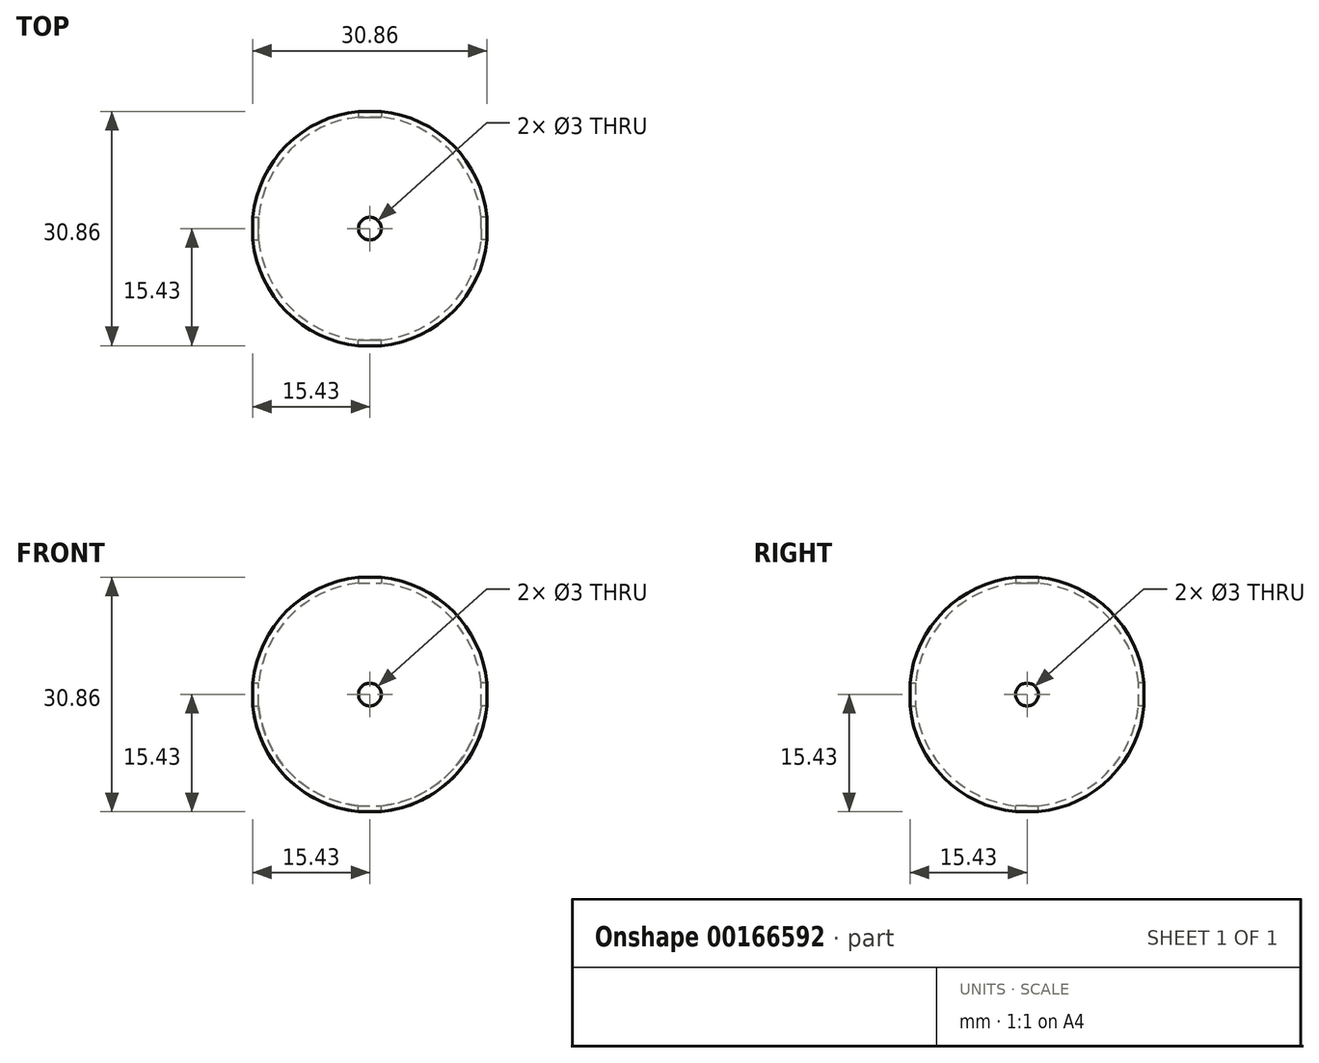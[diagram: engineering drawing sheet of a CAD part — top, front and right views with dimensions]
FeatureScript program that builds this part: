
annotation { "Feature Type Name" : "Feature", "Feature Type Description" : "" }
export const myFeature = defineFeature(function(context is Context, id is Id, definition is map)
    precondition{}
    {
        {
            var Q0;
            Q0=qCreatedBy(makeId("Top.planeOp"),FACE);
            var sketch = newSketch(context, id + "F0", { "sketchPlane" : qUnion([Q0])});
            skLineSegment(sketch, "E0", {"start": v(-18.23, 0) * mm, "end": v(19.4, 0) * mm});
            skArc(sketch, "E1", {"start": v(15.5, 0) * mm, "mid": v(0, 15.5) * mm, "end": v(-15.5, 0) * mm});
            skSolve(sketch);
        }
        {
            var Q0;
            {var subQ0=sQuery(id+"F0.wireOp",EDGE,"E1");Q0=makeQuery(id+"F0.imprint","IMPRINT",FACE,{"disambiguationData":[TD([[makeQuery(id+"F0.imprint","IMPRINT",EDGE,{"derivedFrom":subQ0}),1.0]])]});}
            var Q1;
            Q1 = qSketchRegion(id + "F3", true);
            var Q2;
            Q2=sQuery(id+"F0.wireOp",EDGE,"E0");
            revolve(context, id + "F1", {"entities" : qUnion([Q0, Q1]), "axis" : qUnion([Q2]), "revolveType" : RevolveType.FULL});
        }
        {
            var Q0;
            Q0=makeQuery(id+"F1.opRevolve","SWEPT_FACE",FACE,{"disambiguationData":[OSD([sQuery(id+"F0.wireOp",EDGE,"E1")])]});
            var Q1;
            Q1=makeQuery(id+"F1.opRevolve","SWEPT_BODY",BODY,{"disambiguationData":[OSD([sQuery(id+"F0.wireOp",EDGE,"E0"),sQuery(id+"F0.wireOp",EDGE,"E1")])]});
            shell(context, id + "F2", {"isHollow" : true, "entities" : qUnion([Q0]), "parts" : qUnion([Q1]), "thickness" : .75 * mm});
        }
        {
            var Q0;
            Q0=qCreatedBy(makeId("Top.planeOp"),FACE);
            var sketch = newSketch(context, id + "F3", { "sketchPlane" : qUnion([Q0])});
            skPoint(sketch, "E2", {"position": v(0, 0) * mm});
            skSolve(sketch);
        }
        {
            var Q0;
            Q0=sQuery(id+"F3.wireOp",VERTEX,"E2");
            var Q1;
            Q1=makeQuery(id+"F1.opRevolve","SWEPT_BODY",BODY,{"disambiguationData":[OSD([sQuery(id+"F0.wireOp",EDGE,"E0"),sQuery(id+"F0.wireOp",EDGE,"E1")])]});
            hole(context, id + "F4", {"style" : HoleStyle.SIMPLE, "endStyle" : HoleEndStyle.THROUGH, "holeDiameter" : 3 * mm, "locations" : qUnion([Q0]), "scope" : qUnion([Q1]), "isTappedThrough" : true});
        }
        {
            var Q0;
            Q0=qCreatedBy(makeId("Top.planeOp"),FACE);
            var sketch = newSketch(context, id + "F5", { "sketchPlane" : qUnion([Q0])});
            skPoint(sketch, "E3", {"position": v(0, 0) * mm});
            skSolve(sketch);
        }
        {
            var Q0;
            Q0=sQuery(id+"F5.wireOp",VERTEX,"E3");
            var Q1;
            Q1=makeQuery(id+"F1.opRevolve","SWEPT_BODY",BODY,{"disambiguationData":[OSD([sQuery(id+"F0.wireOp",EDGE,"E0"),sQuery(id+"F0.wireOp",EDGE,"E1")])]});
            hole(context, id + "F6", {"style" : HoleStyle.SIMPLE, "endStyle" : HoleEndStyle.THROUGH, "oppositeDirection" : true, "holeDiameter" : 3 * mm, "locations" : qUnion([Q0]), "scope" : qUnion([Q1]), "isTappedThrough" : true});
        }
        {
            var Q0;
            Q0=qCreatedBy(makeId("Right.planeOp"),FACE);
            var sketch = newSketch(context, id + "F7", { "sketchPlane" : qUnion([Q0])});
            skPoint(sketch, "E4", {"position": v(0, 0) * mm});
            skSolve(sketch);
        }
        {
            var Q0;
            Q0=sQuery(id+"F7.wireOp",VERTEX,"E4");
            var Q1;
            Q1=makeQuery(id+"F1.opRevolve","SWEPT_BODY",BODY,{"disambiguationData":[OSD([sQuery(id+"F0.wireOp",EDGE,"E0"),sQuery(id+"F0.wireOp",EDGE,"E1")])]});
            hole(context, id + "F8", {"style" : HoleStyle.SIMPLE, "endStyle" : HoleEndStyle.THROUGH, "holeDiameter" : 3 * mm, "locations" : qUnion([Q0]), "scope" : qUnion([Q1]), "isTappedThrough" : true});
        }
        {
            var Q0;
            Q0=qCreatedBy(makeId("Right.planeOp"),FACE);
            var sketch = newSketch(context, id + "F9", { "sketchPlane" : qUnion([Q0])});
            skPoint(sketch, "E5", {"position": v(0, 0) * mm});
            skSolve(sketch);
        }
        {
            var Q0;
            Q0=sQuery(id+"F9.wireOp",VERTEX,"E5");
            var Q1;
            Q1=makeQuery(id+"F1.opRevolve","SWEPT_BODY",BODY,{"disambiguationData":[OSD([sQuery(id+"F0.wireOp",EDGE,"E0"),sQuery(id+"F0.wireOp",EDGE,"E1")])]});
            hole(context, id + "F10", {"style" : HoleStyle.SIMPLE, "endStyle" : HoleEndStyle.THROUGH, "oppositeDirection" : true, "holeDiameter" : 3 * mm, "locations" : qUnion([Q0]), "scope" : qUnion([Q1]), "isTappedThrough" : true});
        }
        {
            var Q0;
            Q0=qCreatedBy(makeId("Front.planeOp"),FACE);
            var sketch = newSketch(context, id + "F11", { "sketchPlane" : qUnion([Q0])});
            skPoint(sketch, "E6", {"position": v(0, 0) * mm});
            skSolve(sketch);
        }
        {
            var Q0;
            Q0=sQuery(id+"F11.wireOp",VERTEX,"E6");
            var Q1;
            Q1=makeQuery(id+"F1.opRevolve","SWEPT_BODY",BODY,{"disambiguationData":[OSD([sQuery(id+"F0.wireOp",EDGE,"E0"),sQuery(id+"F0.wireOp",EDGE,"E1")])]});
            hole(context, id + "F12", {"style" : HoleStyle.SIMPLE, "endStyle" : HoleEndStyle.THROUGH, "holeDiameter" : 3 * mm, "locations" : qUnion([Q0]), "scope" : qUnion([Q1]), "isTappedThrough" : true});
        }
        {
            var Q0;
            Q0=qCreatedBy(makeId("Front.planeOp"),FACE);
            var sketch = newSketch(context, id + "F13", { "sketchPlane" : qUnion([Q0])});
            skPoint(sketch, "E7", {"position": v(0, 0) * mm});
            skSolve(sketch);
        }
        {
            var Q0;
            Q0=sQuery(id+"F13.wireOp",VERTEX,"E7");
            var Q1;
            Q1=makeQuery(id+"F1.opRevolve","SWEPT_BODY",BODY,{"disambiguationData":[OSD([sQuery(id+"F0.wireOp",EDGE,"E0"),sQuery(id+"F0.wireOp",EDGE,"E1")])]});
            hole(context, id + "F14", {"style" : HoleStyle.SIMPLE, "endStyle" : HoleEndStyle.THROUGH, "oppositeDirection" : true, "holeDiameter" : 3 * mm, "locations" : qUnion([Q0]), "scope" : qUnion([Q1]), "isTappedThrough" : true});
        }
    });
